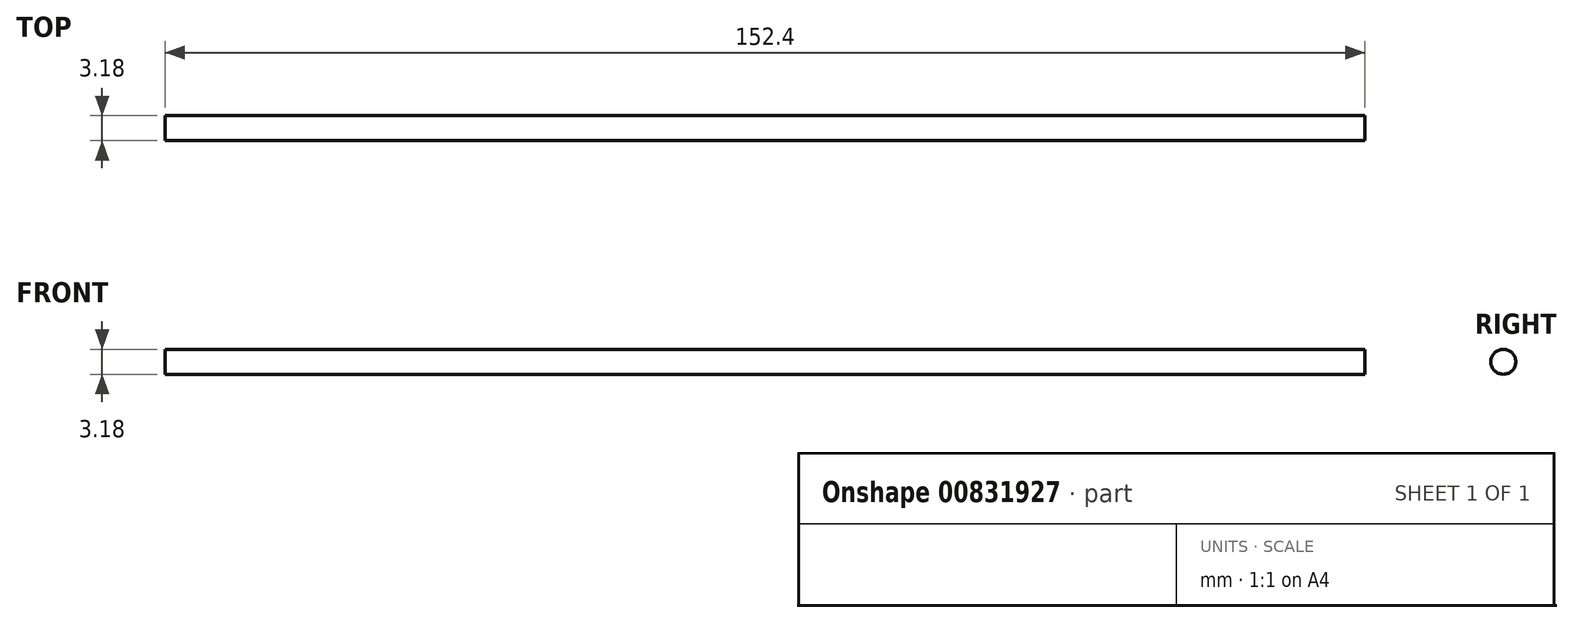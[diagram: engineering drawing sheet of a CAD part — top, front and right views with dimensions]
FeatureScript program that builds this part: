
annotation { "Feature Type Name" : "Feature", "Feature Type Description" : "" }
export const myFeature = defineFeature(function(context is Context, id is Id, definition is map)
    precondition{}
    {
        {
            var Q0;
            Q0=qCreatedBy(makeId("Top.planeOp"),FACE);
            var sketch = newSketch(context, id + "F0", { "sketchPlane" : qUnion([Q0])});
            skLineSegment(sketch, "E0.bottom", {"start": v(-32.1, 14.56) * mm, "end": v(120.3, 14.56) * mm});
            skLineSegment(sketch, "E0.top", {"start": v(-32.1, 12.97) * mm, "end": v(120.3, 12.97) * mm});
            skLineSegment(sketch, "E0.left", {"start": v(-32.1, 14.56) * mm, "end": v(-32.1, 12.97) * mm});
            skLineSegment(sketch, "E0.right", {"start": v(120.3, 14.56) * mm, "end": v(120.3, 12.97) * mm});
            skSolve(sketch);
        }
        {
            var Q0;
            Q0=makeQuery(id+"F0.imprint","IMPRINT",FACE,{"disambiguationData":[TD([[makeQuery(id+"F0.imprint","IMPRINT",EDGE,{"derivedFrom":sQuery(id+"F0.wireOp",EDGE,"E0.bottom")}),-1.0]])]});
            var Q1;
            Q1=sQuery(id+"F0.wireOp",EDGE,"E0.top");
            revolve(context, id + "F1", {"surfaceOperationType" : NewSurfaceOperationType.NEW, "entities" : qUnion([Q0]), "axis" : qUnion([Q1]), "revolveType" : RevolveType.FULL});
        }
    });
